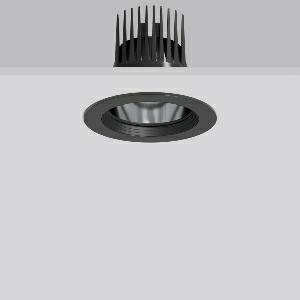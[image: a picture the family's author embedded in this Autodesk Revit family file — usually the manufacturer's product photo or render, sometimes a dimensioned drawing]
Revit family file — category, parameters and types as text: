
# Revit family: heledon_maxi_e_901763_003_547e
name_source: partatom
category: Lighting Fixtures
units: mm (PartAtom-declared; Revit-internal decimal feet)

## family parameters
Cut with Voids When Loaded = No
Host = Face
Light Source = No
Part Type = Normal
Room Calculation Point = No
Round Connector Dimension = Use Diameter
Shared = No

## types (1)
- HELEDON maxi E (1 x LED Modul 930, 4200 lm, 3000)
    Apparent Load = 35 VA
    Approval mark = CE
    CIE Flux Codes = 100 100 100 100 100
    Color Rendering = 90
    Color Temperature = 3000
    Default Elevation = 1800 mm
    Description = Series: HELEDON maxi
Round recessed downlight. Housing: die-cast aluminium, powder-coated. Black plastic ring and recessed LED to prevent glare from the side. Optical assembly with reflector made of MIRO-Silver with 98% total light reflection for outstanding efficiency - can be changed without tools. Best colour rendering index Ra>90. Suitable for Recessed ceiling mounting. Installation without tools thanks to spring fastening system. Including separate LED converter with connecting cable 600 mm.High quality converter without flickering and stroboscopic effect. Through-wiring box (5 pole) available as accessory. The following accessories can be mounted without use of tools: interchangeable lenses, decorative glasses, honeycomb louvre, clear and frosted diffusers, white interchangeable plastic ring. 
Colour: deep black, matt (RAL 9005)
Diameter: 162 mm
Height: 3 mm
Cut-out diameter: 152 mm
Recess height: 200 mm
Luminaire: recess height: 135 mm
Lamp: LED
Socket: without socket
Colour temperature: 3000K
Colour rendering index (CRI): 92
System power: 35 W
Rated luminous flux: 4200 lm
Luminous efficiency: 120 lm/W
Control gear: Regulated power supply
Protection class: II
Type of protection: IP 20
    Height = 0 mm  [stored 0 ft]
    Lamp = 1 x LED Modul 930
    Lamp Light Flux = 4200 lm
    Lamp count = 1
    Length = 162 mm
    Lifetime = 50000 h
    Luminous efficacy = 120 lm/W
    Manufacturer = RZB
    ModVariant = No
    Model = 901763.003
    Mounting Place = Ceiling
    Mounting Type = Recessed
    Number of Poles = 1
    OnlyDefault = Yes
    Power Factor = 1
    Product Name = HELEDON maxi E
    Product group = Recessed downlights
    ProductGroupID = 402
    Protection Class = Protection class II
    Protection Degree = IP 20
    RLX_Detail_Level = 1
    RLX_Emergency_Light_Flux = 0 lm
    RLX_Emergency_Type = 0
    RLX_Emergency_Type_DB = No
    RlxData = <blob elided: 123181 chars, md5=bbeb98fc>
    Socket = socket
    Standby Power = 0 W
    System Light Flux = 4200 lm
    System Power = 35 W
    Type Comments = Product without accessories
    Type Image = 901662.003.jpg
    URL = http://relux.com
    VarID = ---
    Voltage = 230 V
    Voltage Range = 220-240 V
    Weight = 0.00 kg
    Width = 0 mm  [stored 0 ft]

note: [stored X ft] marks values corroborated as IEEE doubles in the binary element streams (Revit-internal decimal feet)

## geometry (parser evidence)
native form markers: Blend x4, Sweep x11
no freeform markers — native parametric forms only
